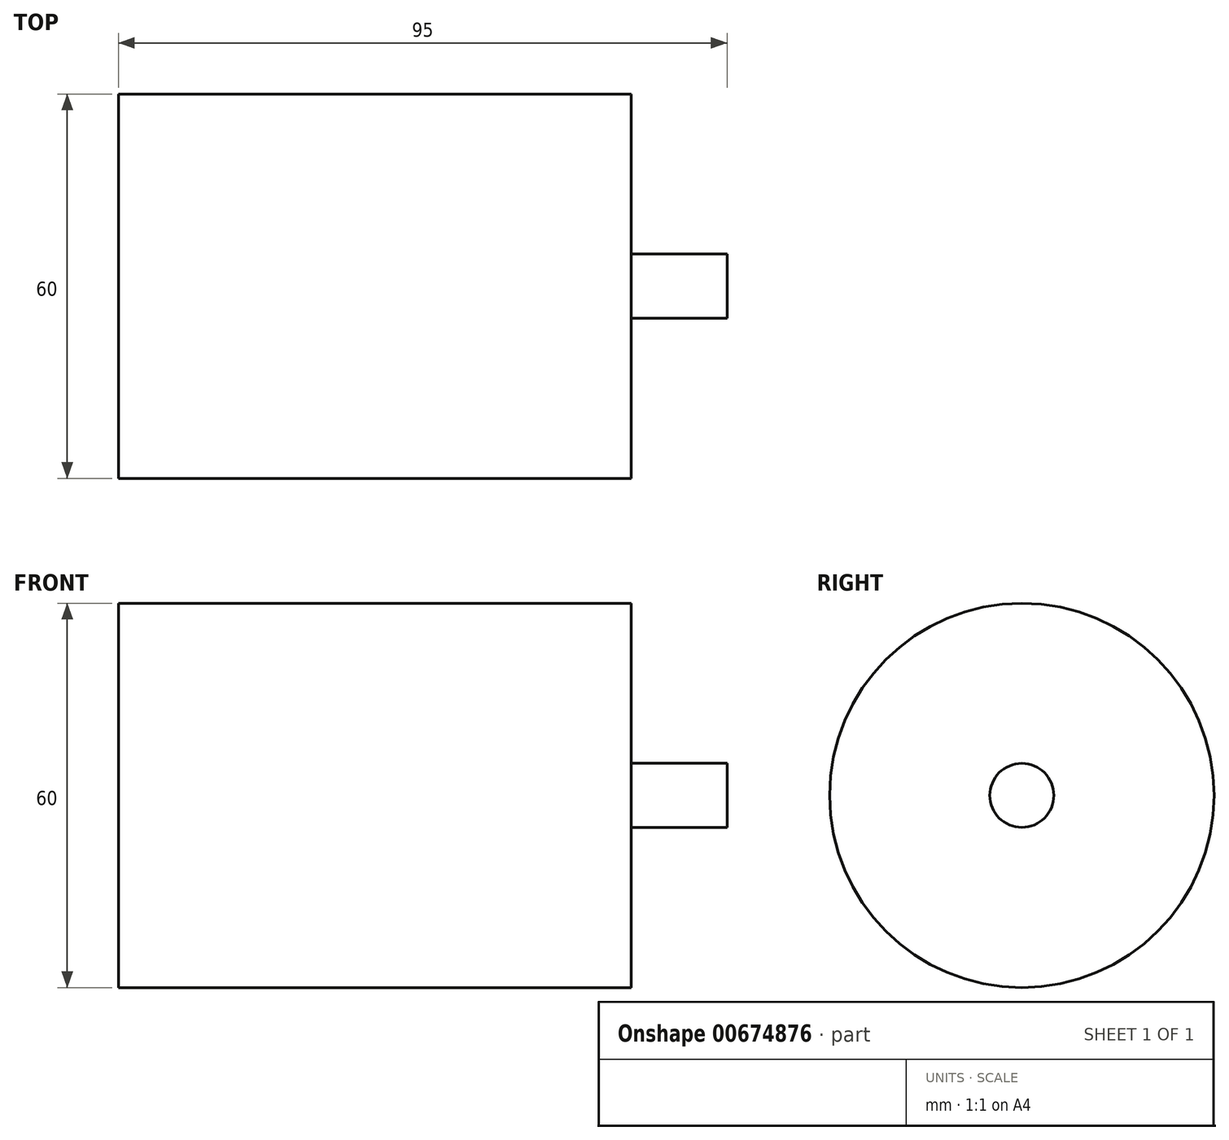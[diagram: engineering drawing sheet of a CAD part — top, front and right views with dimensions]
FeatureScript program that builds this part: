
annotation { "Feature Type Name" : "Feature", "Feature Type Description" : "" }
export const myFeature = defineFeature(function(context is Context, id is Id, definition is map)
    precondition{}
    {
        {
            var Q0;
            Q0=qCreatedBy(makeId("Front.planeOp"),FACE);
            var sketch = newSketch(context, id + "F0", { "sketchPlane" : qUnion([Q0])});
            skLineSegment(sketch, "E0", {"start": v(0, 30) * mm, "end": v(80, 30) * mm});
            skLineSegment(sketch, "E1", {"start": v(80, 30) * mm, "end": v(80, 5) * mm});
            skLineSegment(sketch, "E2", {"start": v(80, 5) * mm, "end": v(95, 5) * mm});
            skLineSegment(sketch, "E3", {"start": v(95, 5) * mm, "end": v(95, 0) * mm});
            skLineSegment(sketch, "E4", {"start": v(95, 0) * mm, "end": v(0, 0) * mm});
            skLineSegment(sketch, "E5", {"start": v(0, 0) * mm, "end": v(0, 30) * mm});
            skLineSegment(sketch, "E6", {"start": v(-20.28, 0) * mm, "end": v(19.4, 0) * mm, "construction": true});
            skSolve(sketch);
        }
        {
            var Q0;
            Q0 = qSketchRegion(id + "F0", true);
            var Q1;
            Q1=sQuery(id+"F0.wireOp",EDGE,"E6");
            revolve(context, id + "F1", {"entities" : qUnion([Q0]), "axis" : qUnion([Q1]), "revolveType" : RevolveType.FULL});
        }
    });
